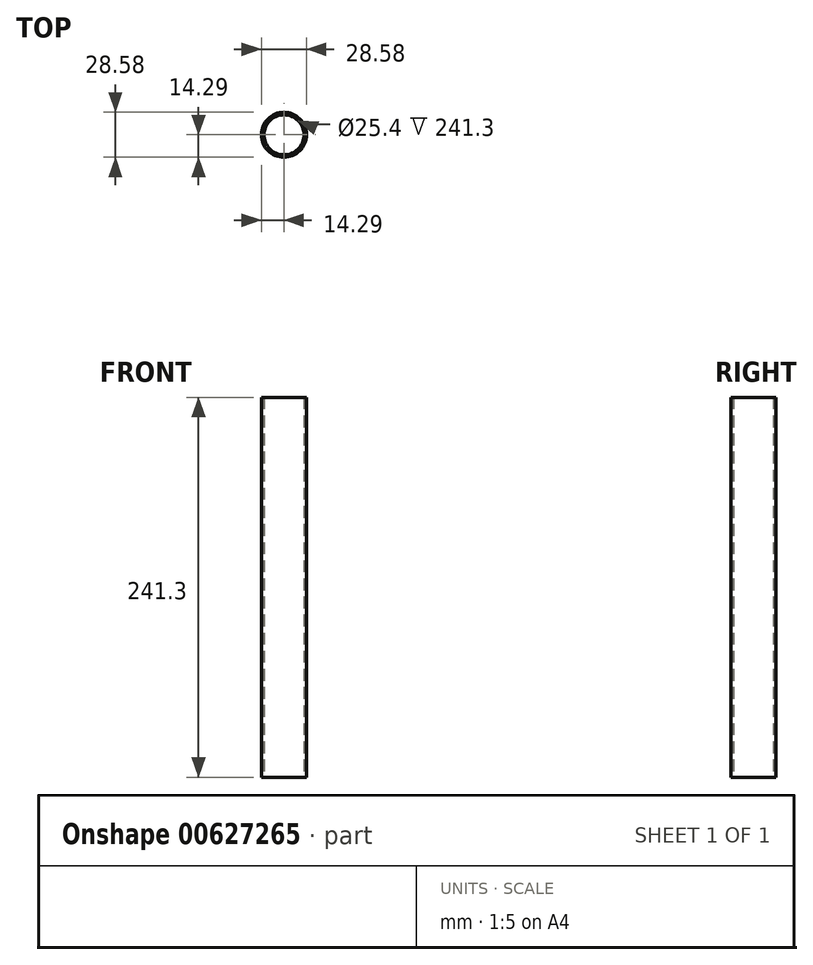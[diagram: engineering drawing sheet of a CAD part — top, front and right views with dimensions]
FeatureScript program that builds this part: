
annotation { "Feature Type Name" : "Feature", "Feature Type Description" : "" }
export const myFeature = defineFeature(function(context is Context, id is Id, definition is map)
    precondition{}
    {
        {
            var Q0;
            Q0=qCreatedBy(makeId("Top.planeOp"),FACE);
            var sketch = newSketch(context, id + "F0", { "sketchPlane" : qUnion([Q0])});
            skLineSegment(sketch, "E0", {"start": v(0, 0) * mm, "end": v(12.7, 0) * mm});
            skCircle(sketch, "E1", {"center": v(0, 0) * mm, "radius": 12.7 * mm});
            skCircle(sketch, "E2.0", {"center": v(0, 0) * mm, "radius": 14.29 * mm});
            skSolve(sketch);
        }
        {
            var Q0;
            Q0=qCreatedBy(makeId("Top.planeOp"),FACE);
            var sketch = newSketch(context, id + "F1", { "sketchPlane" : qUnion([Q0])});
            skSolve(sketch);
        }
        {
            var Q0;
            Q0=qSketchRegion(id+"F1",true);
            var Q1;
            Q1=makeQuery(id+"F0.imprint","IMPRINT",FACE,{"disambiguationData":[TD([[makeQuery(id+"F0.imprint","IMPRINT",EDGE,{"derivedFrom":sQuery(id+"F0.wireOp",EDGE,"E1")}),-1.0]])]});
            extrude(context, id + "F2", {"entities" : qUnion([Q0, Q1]), "depth" : 241.3 * mm, "offsetDistance" : 25.4 * mm});
        }
    });
